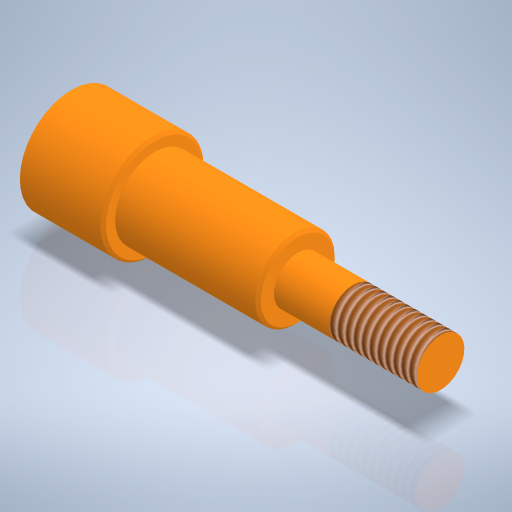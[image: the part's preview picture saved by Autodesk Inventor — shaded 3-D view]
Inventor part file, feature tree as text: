
AUTODESK INVENTOR PART (.ipt)
format: ipt  version: 2024 (Build 280153000, 153)  size: 300,032 bytes
history: native  units: mm
features: sketch x2, revolve x1, thread x1, hole x1, chamfer x1
ambient origin geometry x8: Origin, YZ Plane, XZ Plane, XY Plane, X Axis, Y Axis, Z Axis, Center Point
bodies: Volumenkörper1 (feature_tree)
feature tree (6):
  revolve  "Umdrehung1"
  thread  "Gewinde1"  [1 undecoded]
  hole  "Bohrung1"  [1 undecoded]
  chamfer  "Fasen1"  Distance=10.5mm
  sketch  "Skizze1"  dims[d1=13.0mm d2=10.0mm]
  sketch  "Skizze2"  dims[d3=6.0mm d4=10.5mm d5=18.0mm d6=90.0deg d7=11.0mm d8=0.0mm d9=4.0mm d10=6.0mm d11=4.0mm d12=2.0mm d13=90.0deg d14=26.0mm d15=0.0mm d16=0.35mm d17=2.0mm d18=45.0deg]
note: 2 required parameter values undecoded (feature->parameter linkage not recoverable at this tier; creation-order binding heuristic only, values carry confidence <= 0.55)
